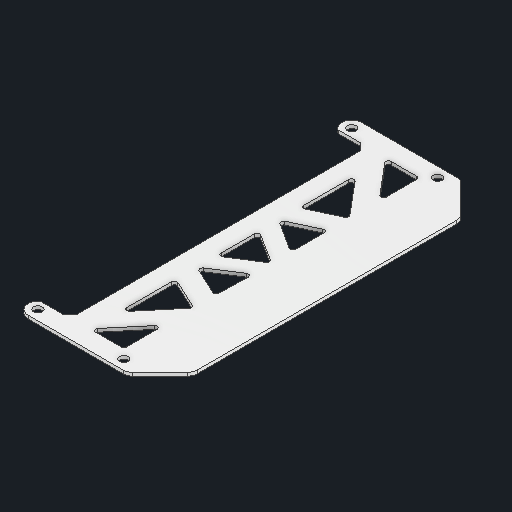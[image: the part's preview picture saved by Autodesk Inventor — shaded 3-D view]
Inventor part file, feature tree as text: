
AUTODESK INVENTOR PART (.ipt)
format: ipt  version: 2025 (Build 290162000, 162)  size: 207,360 bytes
history: native  units: in
note: dims shown in document units (in); Inventor stores cm internally (conversion verified against a paired STEP export)
features: extrude x1, sketch x1
ambient origin geometry x8: Origin, YZ Plane, XZ Plane, XY Plane, X Axis, Y Axis, Z Axis, Center Point
bodies: Solid1 (feature_tree)
feature tree (2):
  extrude  "Extrusion1"  Depth=0.1875in
  sketch  "Sketch1"  dims[d0=0.165in d3=0.375in d9=0.36in d20=0.05in d21=0.0625in d22=0.0in d24=0.875in d27=0.625in d28=0.625in d29=0.625in d30=0.625in d31=0.1875in]
